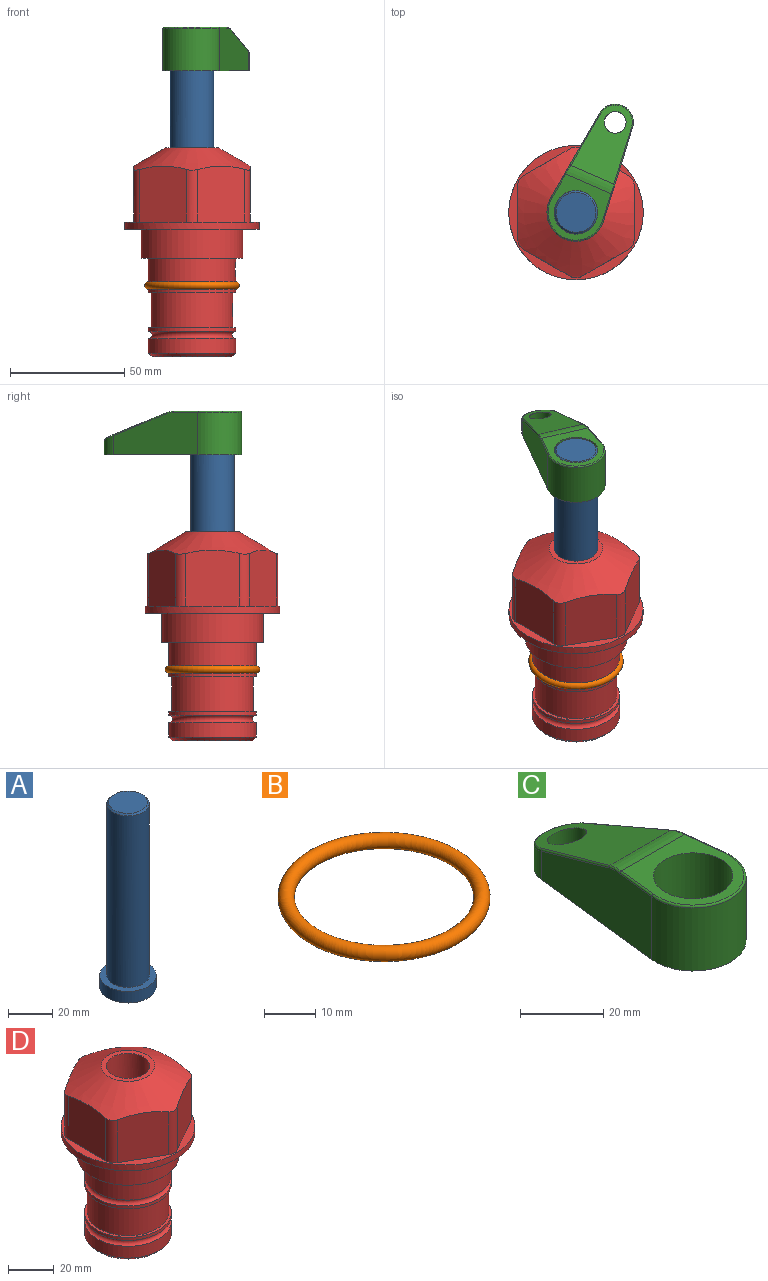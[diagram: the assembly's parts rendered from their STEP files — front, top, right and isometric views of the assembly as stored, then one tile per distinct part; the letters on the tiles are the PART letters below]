
ASSEMBLY  parts=4 mates=2
PART A: 6 faces, bbox 25.4x25.4x101.6 mm
  f0: plane 17.46x17.46mm, normal (0,0,1), area 239.5mm2, adj f5
  f1: plane 25.4x25.4mm, normal (0,0,-1), area 506.7mm2, adj f2
  f2: cylinder r=12.7mm len=25.4mm, axis (0,0,1), area 506.7mm2, adj f1,f3
  f3: plane 25.4x25.4mm, normal (0,0,1), area 221.7mm2, adj f2,f4
  f4: cylinder r=9.53mm len=94.46mm, axis (0,0,1), area 5653mm2, adj f3,f5
  f5: cone r=8.73mm half-angle=45deg, axis (0,0,-1), area 64.4mm2, adj f0,f4
PART B: 1 faces, bbox 44.7x44.7x3.2 mm
  f0: torus R=19.05mm, axis (0,0,1), area 1193.9mm2
PART C: 44 faces, bbox 27.5x64.5x19.1 mm
  f0: plane 2.3x0.95mm, normal (0,0,-1), area 1mm2, adj f25,f30,f34
  f1: plane 63.5x25.4mm, normal (0,0,-1), area 561.7mm2, adj f2,f3,f4,f5,f6,f7,f19,f20
  f2: cylinder r=12.7mm len=25.4mm, axis (0,0,-1), area 792.2mm2, adj f1,f3,f5,f13
  f3: plane 42.33x18.54mm, normal (0.99,0.11,0), area 647mm2, adj f1,f2,f4,f11,f12,f14
  f4: cylinder r=7.94mm len=15.78mm, axis (0,0,-1), area 158.6mm2, adj f1,f3,f5,f16
  f5: plane 42.33x18.54mm, normal (-0.99,0.11,0), area 647mm2, adj f1,f2,f4,f15,f17,f18
  f6: cylinder r=9.53mm len=19.05mm, axis (0,0,-1), area 1140.1mm2, adj f1,f8
  f7: cylinder r=4.76mm len=10.98mm, axis (0,0,-1), area 276.1mm2, adj f1,f9
  f8: plane 25.83x24.38mm, normal (0,0,1), area 262.2mm2, adj f6,f10,f11,f13,f15
  f9: plane 32.49x20.55mm, normal (0,0.34,0.94), area 489.9mm2, adj f7,f10,f14,f16,f18
  f10: cylinder r=12.7mm len=21.49mm, axis (-1,0,0), area 93.2mm2, adj f8,f9,f12,f17
  f11: cylinder r=0.51mm len=12.34mm, axis (0.11,-0.99,0), area 9.9mm2, adj f3,f8,f12,f13
  f12: bspline ~7.62x1.64mm, area 3.5mm2, adj f3,f10,f11,f14
  f13: torus R=12.19mm, axis (0,0,1), area 33.6mm2, adj f2,f8,f11,f15
  f14: cylinder r=0.51mm len=26.01mm, axis (0.1,-0.93,0.34), area 21.6mm2, adj f3,f9,f12,f16
  f15: cylinder r=0.51mm len=12.34mm, axis (0.11,0.99,0), area 9.9mm2, adj f5,f8,f13,f17
  f16: bspline ~15.78x7.05mm, area 15.7mm2, adj f4,f9,f14,f18
  f17: bspline ~7.62x1.64mm, area 3.5mm2, adj f5,f10,f15,f18
  f18: cylinder r=0.51mm len=26.01mm, axis (0.1,0.93,-0.34), area 21.6mm2, adj f5,f9,f16,f17
  f19: plane 21.6x14.29mm, normal (-0.99,-0.11,0), area 242.6mm2, adj f1,f26,f28,f34,f36,f38
  f20: plane 21.6x14.29mm, normal (0.99,-0.11,0), area 242.6mm2, adj f1,f27,f29,f37,f39,f41
  f21: cylinder r=12.7mm len=14.29mm, axis (0,0,-1), area 173.2mm2, adj f1,f26,f27,f30,f31,f33
  f22: cylinder r=7.94mm len=7.63mm, axis (0,0,-1), area 53.8mm2, adj f1,f28,f29,f42
  f23: plane 2.3x0.95mm, normal (0,0,-1), area 1mm2, adj f25,f33,f37
  f24: plane 17.94x12.32mm, normal (0,-0.34,-0.94), area 191.2mm2, adj f25,f38,f41,f42
  f25: cylinder r=9.53mm len=12.93mm, axis (-1,0,0), area 37.5mm2, adj f0,f23,f24,f31,f36,f39
  f26: cylinder r=1.59mm len=14.29mm, axis (0,0,-1), area 49mm2, adj f1,f19,f21,f32
  f27: cylinder r=1.59mm len=14.29mm, axis (0,0,-1), area 49mm2, adj f1,f20,f21,f35
  f28: cylinder r=1.59mm len=7.28mm, axis (0,0,-1), area 22.1mm2, adj f1,f19,f22,f40
  f29: cylinder r=1.59mm len=7.28mm, axis (0,0,-1), area 22.1mm2, adj f1,f20,f22,f43
  f30: torus R=14.29mm, axis (0,0,1), area 5.8mm2, adj f0,f21,f31,f32
  f31: bspline ~11.06x2.73mm, area 20.8mm2, adj f21,f25,f30,f33
  f32: sphere r=1.59mm, area 5.4mm2, adj f26,f30,f34
  f33: torus R=14.29mm, axis (0,0,1), area 5.8mm2, adj f21,f23,f31,f35
  f34: cylinder r=1.59mm len=1.68mm, axis (-0.11,0.99,0), area 2.4mm2, adj f0,f19,f32,f36
  f35: sphere r=1.59mm, area 5.4mm2, adj f27,f33,f37
  f36: bspline ~5.82x2.33mm, area 7.7mm2, adj f19,f25,f34,f38
  f37: cylinder r=1.59mm len=1.68mm, axis (0.11,0.99,0), area 2.4mm2, adj f20,f23,f35,f39
  f38: cylinder r=1.59mm len=18.33mm, axis (0.1,-0.93,0.34), area 46.7mm2, adj f19,f24,f36,f40
  f39: bspline ~5.82x2.33mm, area 7.7mm2, adj f20,f25,f37,f41
  f40: sphere r=1.59mm, area 3.6mm2, adj f28,f38,f42
  f41: cylinder r=1.59mm len=18.33mm, axis (0.1,0.93,-0.34), area 46.7mm2, adj f20,f24,f39,f43
  f42: bspline ~8.31x1.84mm, area 15.3mm2, adj f22,f24,f40,f43
  f43: sphere r=1.59mm, area 3.6mm2, adj f29,f41,f42
PART D: 36 faces, bbox 58.7x58.7x91.2 mm
  f0: cylinder r=17.78mm len=35.56mm, axis (0,0,1), area 1670.8mm2, adj f23,f24,f31
  f1: cylinder r=19.05mm len=38.1mm, axis (0,0,1), area 1191.9mm2, adj f26,f27,f30
  f2: plane 58.66x58.66mm, normal (0,0,-1), area 1150.6mm2, adj f3,f28
  f3: cylinder r=29.33mm len=58.66mm, axis (0,0,-1), area 585.1mm2, adj f2,f4
  f4: plane 58.66x58.66mm, normal (0,0,1), area 475.9mm2, adj f3,f5,f6,f7,f8,f9,f10,f11
  f5: plane 24.5x20.32mm, normal (-0.5,0.87,0), area 562.8mm2, adj f4,f15,f16,f17
  f6: plane 24.5x20.32mm, normal (0.5,0.87,0), area 562.8mm2, adj f4,f14,f15,f17
  f7: plane 24.5x23.48mm, normal (1,0,0), area 562.8mm2, adj f4,f13,f14,f17
  f8: plane 24.5x20.32mm, normal (0.5,-0.87,0), area 562.8mm2, adj f4,f12,f13,f17
  f9: plane 24.5x20.32mm, normal (-0.5,-0.87,0), area 562.8mm2, adj f4,f11,f12,f17
  f10: plane 24.5x23.48mm, normal (-1,0,0), area 562.8mm2, adj f4,f11,f16,f17
  f11: cylinder r=5.08mm len=23.01mm, axis (0,0,-1), area 121.2mm2, adj f4,f9,f10,f17
  f12: cylinder r=5.08mm len=23.01mm, axis (0,0,-1), area 121.2mm2, adj f4,f8,f9,f17
  f13: cylinder r=5.08mm len=23.01mm, axis (0,0,-1), area 121.2mm2, adj f4,f7,f8,f17
  f14: cylinder r=5.08mm len=23.01mm, axis (0,0,-1), area 121.2mm2, adj f4,f6,f7,f17
  f15: cylinder r=5.08mm len=23.01mm, axis (0,0,-1), area 121.2mm2, adj f4,f5,f6,f17
  f16: cylinder r=5.08mm len=23.01mm, axis (0,0,-1), area 121.2mm2, adj f4,f5,f10,f17
  f17: cone r=11.73mm half-angle=60deg, axis (0,0,-1), area 2071.8mm2, adj f5,f6,f7,f8,f9,f10,f11,f12
  f18: plane 23.46x23.46mm, normal (0,0,1), area 147.4mm2, adj f17,f35
  f19: plane 34.93x34.93mm, normal (0,0,-1), area 958mm2, adj f29
  f20: cylinder r=19.05mm len=38.1mm, axis (0,0,1), area 760.1mm2, adj f21,f29
  f21: torus R=19.05mm, axis (0,0,1), area 565.3mm2, adj f20,f22
  f22: cylinder r=19.05mm len=38.1mm, axis (0,0,1), area 190mm2, adj f21,f23
  f23: plane 38.1x38.1mm, normal (0,0,1), area 146.9mm2, adj f0,f22
  f24: plane 38.1x38.1mm, normal (0,0,-1), area 146.9mm2, adj f0,f25
  f25: cylinder r=19.05mm len=38.1mm, axis (0,0,1), area 190mm2, adj f24,f26
  f26: torus R=19.05mm, axis (0,0,1), area 565.3mm2, adj f1,f25
  f27: plane 44.45x44.45mm, normal (0,0,-1), area 411.7mm2, adj f1,f28
  f28: cylinder r=22.23mm len=44.45mm, axis (0,0,1), area 1773.5mm2, adj f2,f27
  f29: cone r=19.05mm half-angle=45deg, axis (0,0,1), area 257.5mm2, adj f19,f20
  f30: cylinder r=3.17mm len=6.75mm, axis (-1,0,0), area 128mm2, adj f1,f33
  f31: cylinder r=3.17mm len=6.35mm, axis (-1,0,0), area 102.5mm2, adj f0,f33
  f32: plane 25.4x25.4mm, normal (0,0,1), area 506.7mm2, adj f33
  f33: cylinder r=12.7mm len=66.42mm, axis (0,0,-1), area 5236.2mm2, adj f30,f31,f32,f34
  f34: cone r=9.53mm half-angle=30deg, axis (0,0,-1), area 443.4mm2, adj f33,f35
  f35: cylinder r=9.53mm len=19.05mm, axis (0,0,-1), area 849mm2, adj f18,f34
PLACE A rot(axis=(0,0,-1),23.5deg) t=(0,0,14.62)mm
PLACE B at identity
PLACE C rot(axis=(0,0,-1),23.5deg) t=(0,0,69.23)mm
PLACE D at identity fixed
MATE fastened C.f2 <-> A.f2  axis (0,0,-1) through (0,0,88.28)mm
MATE cylindrical A.f2 <-> D.f0  axis (0,0,1) through (0,0,40.26)mm
